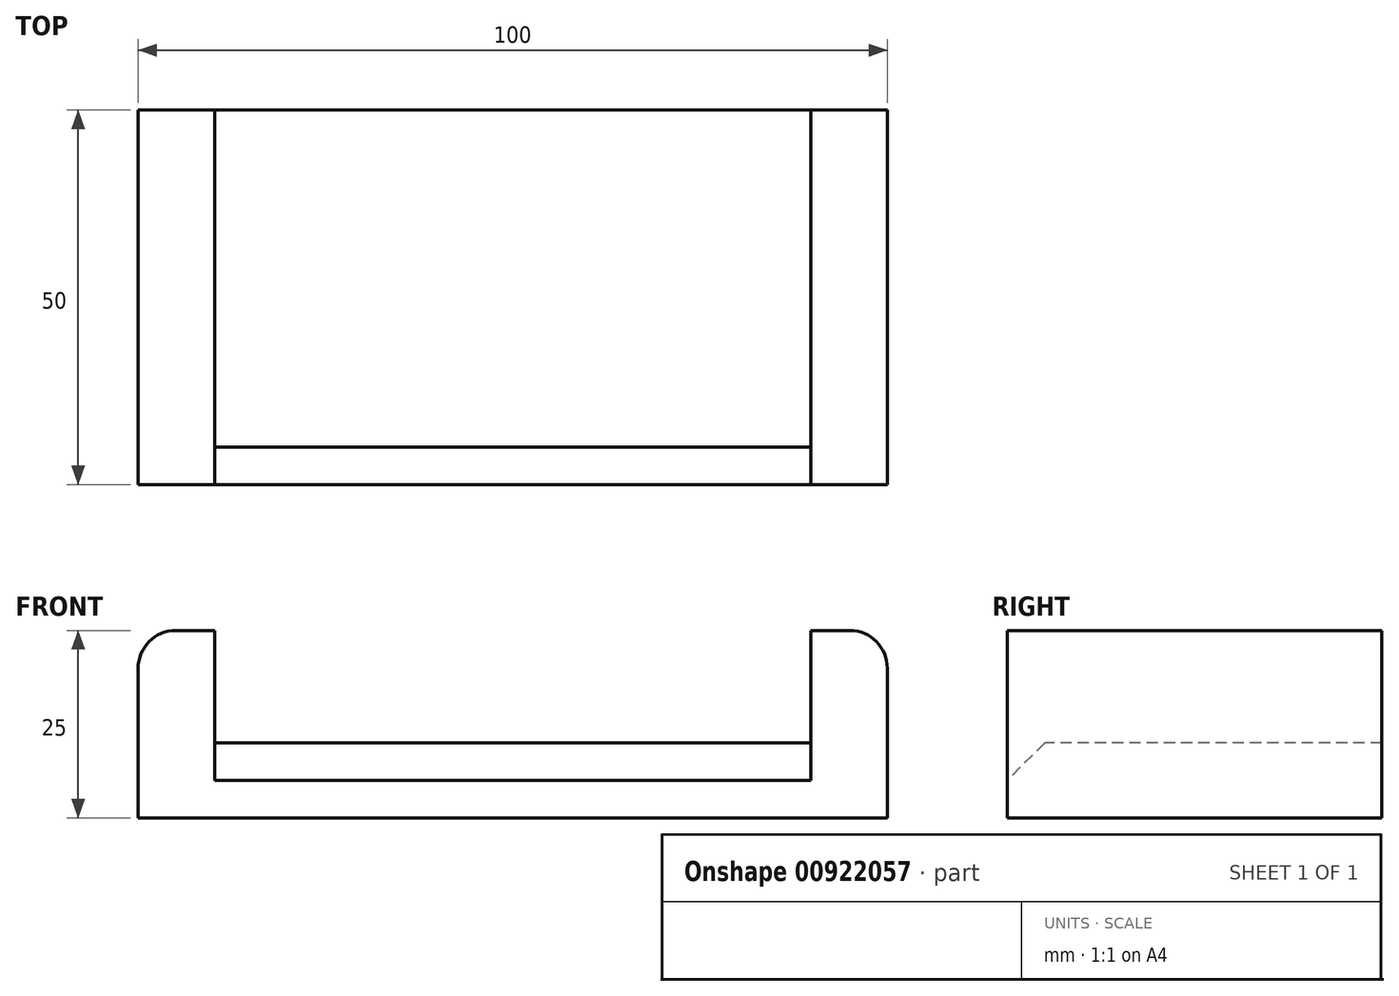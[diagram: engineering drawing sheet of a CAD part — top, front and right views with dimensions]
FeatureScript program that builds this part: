
annotation { "Feature Type Name" : "Feature", "Feature Type Description" : "" }
export const myFeature = defineFeature(function(context is Context, id is Id, definition is map)
    precondition{}
    {
        {
            var Q0;
            Q0=qCreatedBy(makeId("Top.planeOp"),FACE);
            var sketch = newSketch(context, id + "F0", { "sketchPlane" : qUnion([Q0])});
            skLineSegment(sketch, "E0.bottom", {"start": v(50, 25) * mm, "end": v(-50, 25) * mm});
            skLineSegment(sketch, "E0.top", {"start": v(50, -25) * mm, "end": v(-50, -25) * mm});
            skLineSegment(sketch, "E0.left", {"start": v(50, 25) * mm, "end": v(50, -25) * mm});
            skLineSegment(sketch, "E0.right", {"start": v(-50, 25) * mm, "end": v(-50, -25) * mm});
            skPoint(sketch, "E0.middle", {"position": v(0, 0) * mm});
            skLineSegment(sketch, "E1.bottom", {"start": v(-50, 25) * mm, "end": v(-39.78, 25) * mm});
            skLineSegment(sketch, "E1.top", {"start": v(-50, -25) * mm, "end": v(-39.78, -25) * mm});
            skLineSegment(sketch, "E1.right", {"start": v(-39.78, 25) * mm, "end": v(-39.78, -25) * mm});
            skLineSegment(sketch, "E2.MirrorCS", {"start": v(39.78, 25) * mm, "end": v(39.78, -25) * mm});
            skSolve(sketch);
        }
        {
            var Q0;
            {var subQ0=sQuery(id+"F0.wireOp",EDGE,"E0.right");Q0=makeQuery(id+"F0.imprint","IMPRINT",FACE,{"disambiguationData":[TD([[makeQuery(id+"F0.imprint","IMPRINT",EDGE,{"derivedFrom":subQ0}),1.0]])]});}
            extrude(context, id + "F1", {"entities" : qUnion([Q0]), "depth" : 25 * mm, "offsetDistance" : 25 * mm});
        }
        {
            var Q0;
            {var subQ2=sQuery(id+"F0.wireOp",EDGE,"E1.right");Q0=makeQuery(id+"F0.imprint","IMPRINT",FACE,{"disambiguationData":[TD([[makeQuery(id+"F0.imprint","IMPRINT",EDGE,{"derivedFrom":subQ2}),1.0]])]});}
            extrude(context, id + "F2", {"entities" : qUnion([Q0]), "operationType" : NewBodyOperationType.ADD, "depth" : 10 * mm, "offsetDistance" : 25 * mm});
        }
        {
            var Q0;
            {var subQ2=sQuery(id+"F0.wireOp",EDGE,"E0.left");Q0=makeQuery(id+"F0.imprint","IMPRINT",FACE,{"disambiguationData":[TD([[makeQuery(id+"F0.imprint","IMPRINT",EDGE,{"derivedFrom":subQ2}),-1.0]])]});}
            extrude(context, id + "F3", {"entities" : qUnion([Q0]), "operationType" : NewBodyOperationType.ADD, "depth" : 25 * mm, "offsetDistance" : 25 * mm});
        }
        {
            var Q0;
            Q0=makeQuery(id+"F3.opExtrude","CAP_EDGE",EDGE,{"disambiguationData":[OSD([sQuery(id+"F0.wireOp",EDGE,"E0.left")])],"isStart":false});
            fillet(context, id + "F4", {"entities" : qUnion([Q0]), "radius" : 5 * mm, "tangentPropagation" : true, "allowEdgeOverflow" : false});
        }
        {
            var Q0;
            Q0=makeQuery(id+"F1.opExtrude","CAP_EDGE",EDGE,{"disambiguationData":[OSD([sQuery(id+"F0.wireOp",EDGE,"E0.right")])],"isStart":false});
            fillet(context, id + "F5", {"entities" : qUnion([Q0]), "radius" : 5 * mm, "tangentPropagation" : true, "allowEdgeOverflow" : false});
        }
        {
            var Q0;
            Q0=makeQuery(id+"F2.opExtrude","CAP_EDGE",EDGE,{"disambiguationData":[OSD([sQuery(id+"F0.wireOp",EDGE,"E0.top")])],"isStart":false});
            chamfer(context, id + "F6", {"entities" : qUnion([Q0]), "width" : 5 * mm, "tangentPropagation" : true});
        }
    });
